# Revit family: Faucet-Single_Hole-Grohe-34702_Series
name_source: partatom
category: Plumbing Fixtures
revit_build: Autodesk Revit 2018 (Build: 20170223_1515(x64)
units: mm (PartAtom-declared; Revit-internal decimal feet)

## family parameters
Always vertical = No
Cut with Voids When Loaded = No
OmniClass Number = 23.45.55.17
OmniClass Title = Mixing Faucets
Part Type = Normal
Room Calculation Point = No
Round Connector Dimension = Use Diameter
Shared = Yes
Work Plane-Based = Yes

## types (2) — shared parameters
Assembly Code = D2020300
CW Connection = Yes
CWFU = 1.5
Cold Water Connection Diameter = 1/2"
Default Elevation = 0"
Description = Single-Handle Bathroom Faucet XS-Size
Flow Rate = 1.2 gpm
HW Connection = Yes
HWFU = 1.5
Height = 4 23/32"
Hot Water Connection Diameter = 1"
Installation Type = Deck-Mounted
Length = 5 7/8"
Manufacturer = Grohe
Price = Prices may vary. Please consult Manufacturer Representative for most up-to-date price list.
Product Documentation Link = https://americanstandard.box.com
Product Page URL = https://www.grohe.us
Region = North America
URL = https://www.grohe.us
Vent Connection = No
WFU = 2
Warranty Information = Limited Lifetime Warranty
Waste Connection = No
Width = 1 7/8"

## per-type parameters (varying)
| type | Body Material | Material |
| 34702001 | Metal-Grohe-001-Starlight Chrome | Metal-Grohe-001-Starlight Chrome |
| 34702EN1 | Metal-Grohe-EN1-Brushed Nickel Infinity Finish | Metal-Grohe-EN1-Brushed Nickel Infinity Finish |

note: column(s) folded — value = type name in every type: Model

## geometry (parser evidence)
native form markers: Sweep x2
no freeform markers — native parametric forms only
